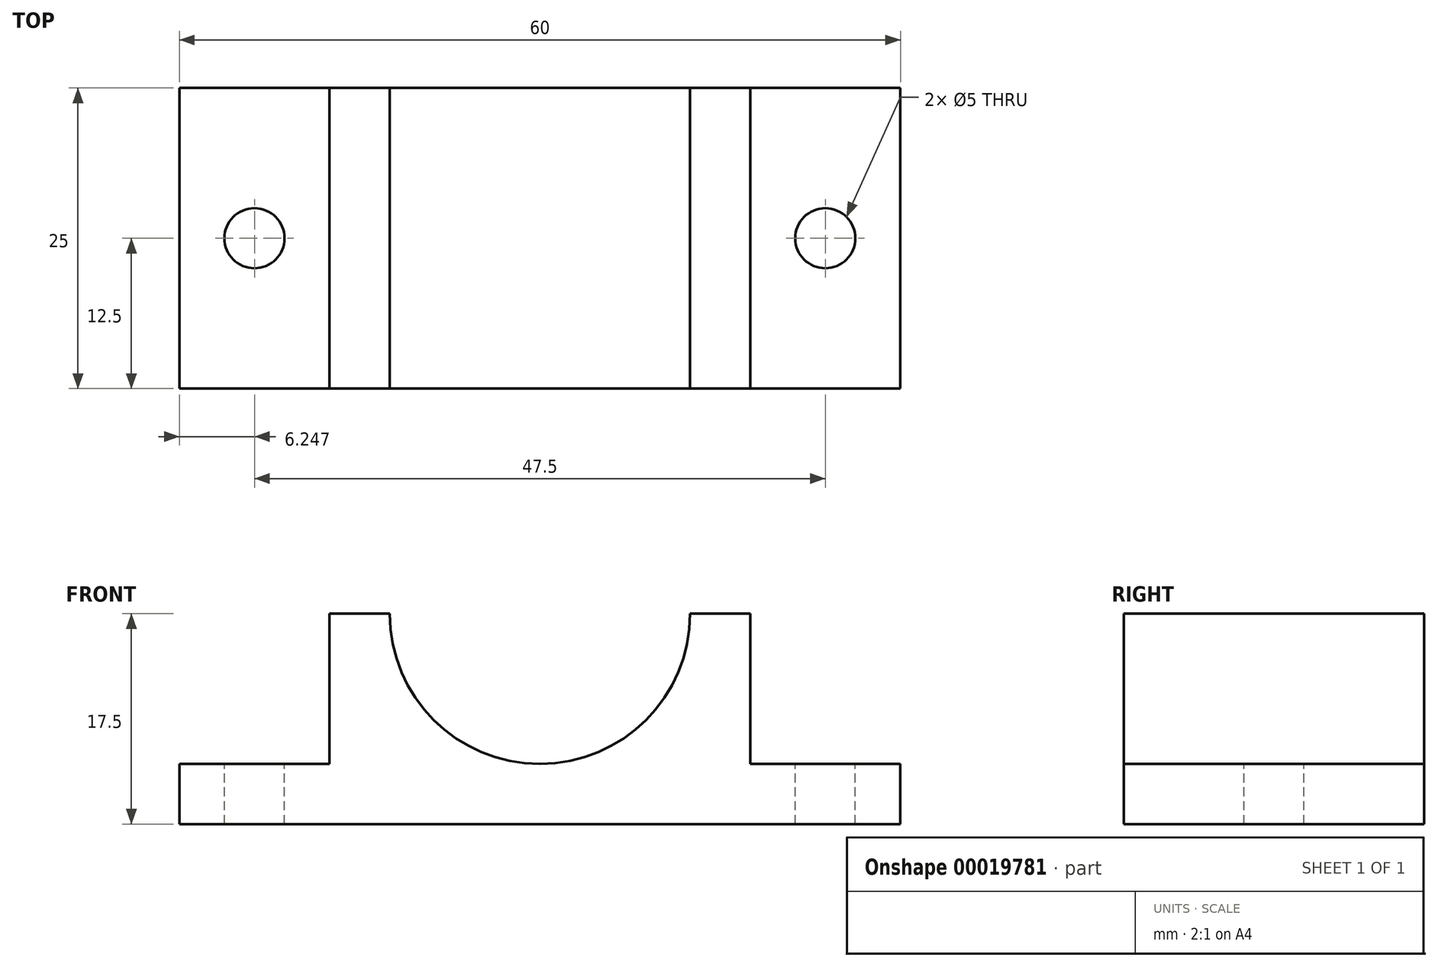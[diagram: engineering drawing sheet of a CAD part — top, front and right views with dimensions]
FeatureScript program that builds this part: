
annotation { "Feature Type Name" : "Feature", "Feature Type Description" : "" }
export const myFeature = defineFeature(function(context is Context, id is Id, definition is map)
    precondition{}
    {
        {
            var Q0;
            Q0=qCreatedBy(makeId("Front.planeOp"),FACE);
            var sketch = newSketch(context, id + "F0", { "sketchPlane" : qUnion([Q0])});
            skLineSegment(sketch, "E0", {"start": v(-31.06, -15.54) * mm, "end": v(-31.06, -10.54) * mm});
            skLineSegment(sketch, "E1", {"start": v(-31.06, -10.54) * mm, "end": v(-18.56, -10.54) * mm});
            skLineSegment(sketch, "E2", {"start": v(-18.56, -10.54) * mm, "end": v(-18.56, 1.96) * mm});
            skLineSegment(sketch, "E3", {"start": v(-18.56, 1.96) * mm, "end": v(16.44, 1.96) * mm});
            skLineSegment(sketch, "E4", {"start": v(16.44, 1.96) * mm, "end": v(16.44, -10.54) * mm});
            skLineSegment(sketch, "E5", {"start": v(16.44, -10.54) * mm, "end": v(28.94, -10.54) * mm});
            skLineSegment(sketch, "E6", {"start": v(28.94, -10.54) * mm, "end": v(28.94, -15.54) * mm});
            skLineSegment(sketch, "E7", {"start": v(28.94, -15.54) * mm, "end": v(-31.06, -15.54) * mm});
            skSolve(sketch);
        }
        {
            var Q0;
            Q0=makeQuery(id+"F0.imprint","IMPRINT",FACE,{"disambiguationData":[TD([[makeQuery(id+"F0.imprint","IMPRINT",EDGE,{"derivedFrom":sQuery(id+"F0.wireOp",EDGE,"E0")}),-1.0]])]});
            extrude(context, id + "F1", {"entities" : qUnion([Q0]), "oppositeDirection" : true, "depth" : 25 * mm});
        }
        {
            var Q0;
            Q0=makeQuery(id+"F1.opExtrude","SWEPT_FACE",FACE,{"disambiguationData":[OSD([sQuery(id+"F0.wireOp",EDGE,"E1")])]});
            var sketch = newSketch(context, id + "F2", { "sketchPlane" : qUnion([Q0])});
            skCircle(sketch, "E8", {"center": v(-24.81, 12.5) * mm, "radius": 2.5 * mm});
            skSolve(sketch);
        }
        {
            var Q0;
            Q0=makeQuery(id+"F2.imprint","IMPRINT",FACE,{"disambiguationData":[TD([[makeQuery(id+"F2.imprint","IMPRINT",EDGE,{"derivedFrom":sQuery(id+"F2.wireOp",EDGE,"E8")}),1.0]])]});
            extrude(context, id + "F3", {"entities" : qUnion([Q0]), "operationType" : NewBodyOperationType.REMOVE, "oppositeDirection" : true, "depth" : 25 * mm});
        }
        {
            var Q0;
            Q0=makeQuery(id+"F1.opExtrude","SWEPT_FACE",FACE,{"disambiguationData":[OSD([sQuery(id+"F0.wireOp",EDGE,"E5")])]});
            var sketch = newSketch(context, id + "F4", { "sketchPlane" : qUnion([Q0])});
            skCircle(sketch, "E9", {"center": v(22.69, 12.5) * mm, "radius": 2.5 * mm});
            skSolve(sketch);
        }
        {
            var Q0;
            Q0=makeQuery(id+"F4.imprint","IMPRINT",FACE,{"disambiguationData":[TD([[makeQuery(id+"F4.imprint","IMPRINT",EDGE,{"derivedFrom":sQuery(id+"F4.wireOp",EDGE,"E9")}),1.0]])]});
            extrude(context, id + "F5", {"entities" : qUnion([Q0]), "operationType" : NewBodyOperationType.REMOVE, "oppositeDirection" : true, "depth" : 25 * mm});
        }
        {
            var Q0;
            Q0=makeQuery(id+"F1.opExtrude","CAP_FACE",FACE,{"disambiguationData":[OSD([sQuery(id+"F0.wireOp",EDGE,"E0"),sQuery(id+"F0.wireOp",EDGE,"E1"),sQuery(id+"F0.wireOp",EDGE,"E2"),sQuery(id+"F0.wireOp",EDGE,"E3"),sQuery(id+"F0.wireOp",EDGE,"E4"),sQuery(id+"F0.wireOp",EDGE,"E5"),sQuery(id+"F0.wireOp",EDGE,"E6"),sQuery(id+"F0.wireOp",EDGE,"E7")])],"isStart":true});
            var sketch = newSketch(context, id + "F6", { "sketchPlane" : qUnion([Q0])});
            skArc(sketch, "E10", {"start": v(-13.56, 1.96) * mm, "mid": v(-1.06, -10.54) * mm, "end": v(11.44, 1.96) * mm});
            skSolve(sketch);
        }
        {
            var Q0;
            {var subQ1=sQuery(id+"F6.wireOp",EDGE,"E10");Q0=makeQuery(id+"F6.imprint","IMPRINT",FACE,{"disambiguationData":[TD([[makeQuery(id+"F6.imprint","IMPRINT",EDGE,{"derivedFrom":subQ1}),1.0]])]});}
            extrude(context, id + "F7", {"entities" : qUnion([Q0]), "operationType" : NewBodyOperationType.REMOVE, "oppositeDirection" : true, "depth" : 25 * mm});
        }
    });
